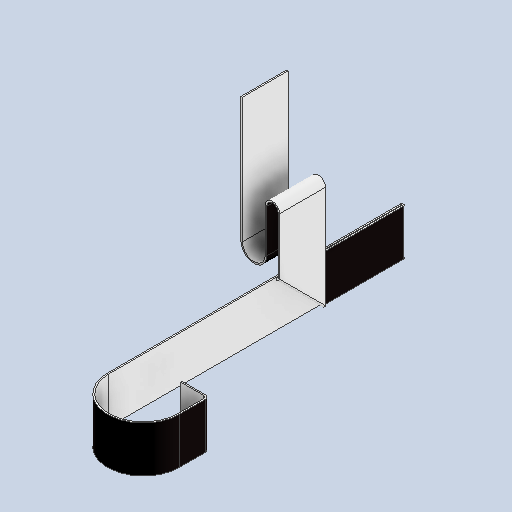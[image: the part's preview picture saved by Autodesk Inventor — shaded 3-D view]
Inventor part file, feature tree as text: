
AUTODESK INVENTOR PART (.ipt)
format: ipt  version: 2024.2 (Build 282272000, 272)  size: 208,896 bytes
history: native  units: mm
features: other x6, sketch x5, extrude x1
ambient origin geometry x8: Origin, YZ Plane, XZ Plane, XY Plane, X Axis, Y Axis, Z Axis, Center Point
bodies: Solid1 (feature_tree)
feature tree (12):
  extrude  "Extrusion1"  Depth=16.0mm
  other  "Bend Part1"
  other  "Bend Part13"
  other  "Bend Part14"
  other  "Bend Part15"
  other  "Bend Part16"
  other  "Bend Part17"
  sketch  "Sketch2"  dims[d0=300.0mm d1=16.0mm]
  sketch  "Sketch16"  dims[d2=0.5mm d3=0.0mm]
  sketch  "Sketch18"  dims[d4=8.0mm]
  sketch  "Sketch19"  dims[d5=1.0mm d6=90.0deg]
  sketch  "Sketch20"  dims[d50=10.0mm d51=12.0mm d52=180.0deg d53=45.0deg d54=130.0mm d55=0.1mm d56=180.0deg d57=28.0mm d58=0.1mm d59=180.0deg d60=20.0mm d61=2.0mm d62=180.0deg d63=15.0mm d64=4.0mm d65=180.0deg]
